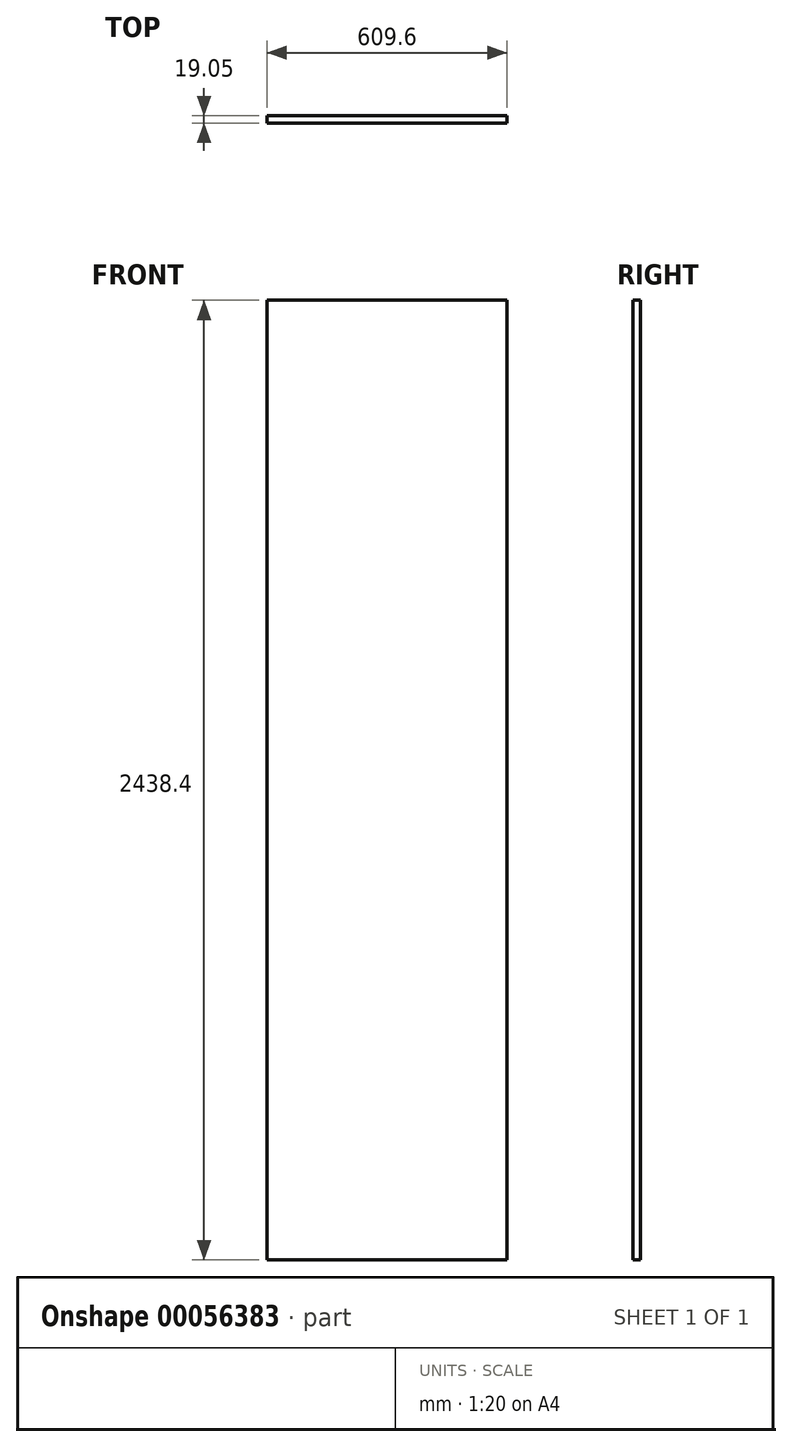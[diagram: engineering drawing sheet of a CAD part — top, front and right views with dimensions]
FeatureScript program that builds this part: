
annotation { "Feature Type Name" : "Feature", "Feature Type Description" : "" }
export const myFeature = defineFeature(function(context is Context, id is Id, definition is map)
    precondition{}
    {
        {
            var Q0;
            Q0=qCreatedBy(makeId("Front.planeOp"),FACE);
            var sketch = newSketch(context, id + "F0", { "sketchPlane" : qUnion([Q0])});
            skLineSegment(sketch, "E0.bottom", {"start": v(-313.2, 1766.93) * mm, "end": v(296.4, 1766.93) * mm});
            skLineSegment(sketch, "E0.top", {"start": v(-313.2, -671.47) * mm, "end": v(296.4, -671.47) * mm});
            skLineSegment(sketch, "E0.left", {"start": v(-313.2, 1766.93) * mm, "end": v(-313.2, -671.47) * mm});
            skLineSegment(sketch, "E0.right", {"start": v(296.4, 1766.93) * mm, "end": v(296.4, -671.47) * mm});
            skSolve(sketch);
        }
        {
            var Q0;
            Q0 = qSketchRegion(id + "F0", true);
            extrude(context, id + "F1", {"entities" : qUnion([Q0]), "depth" : 19.05 * mm});
        }
    });
